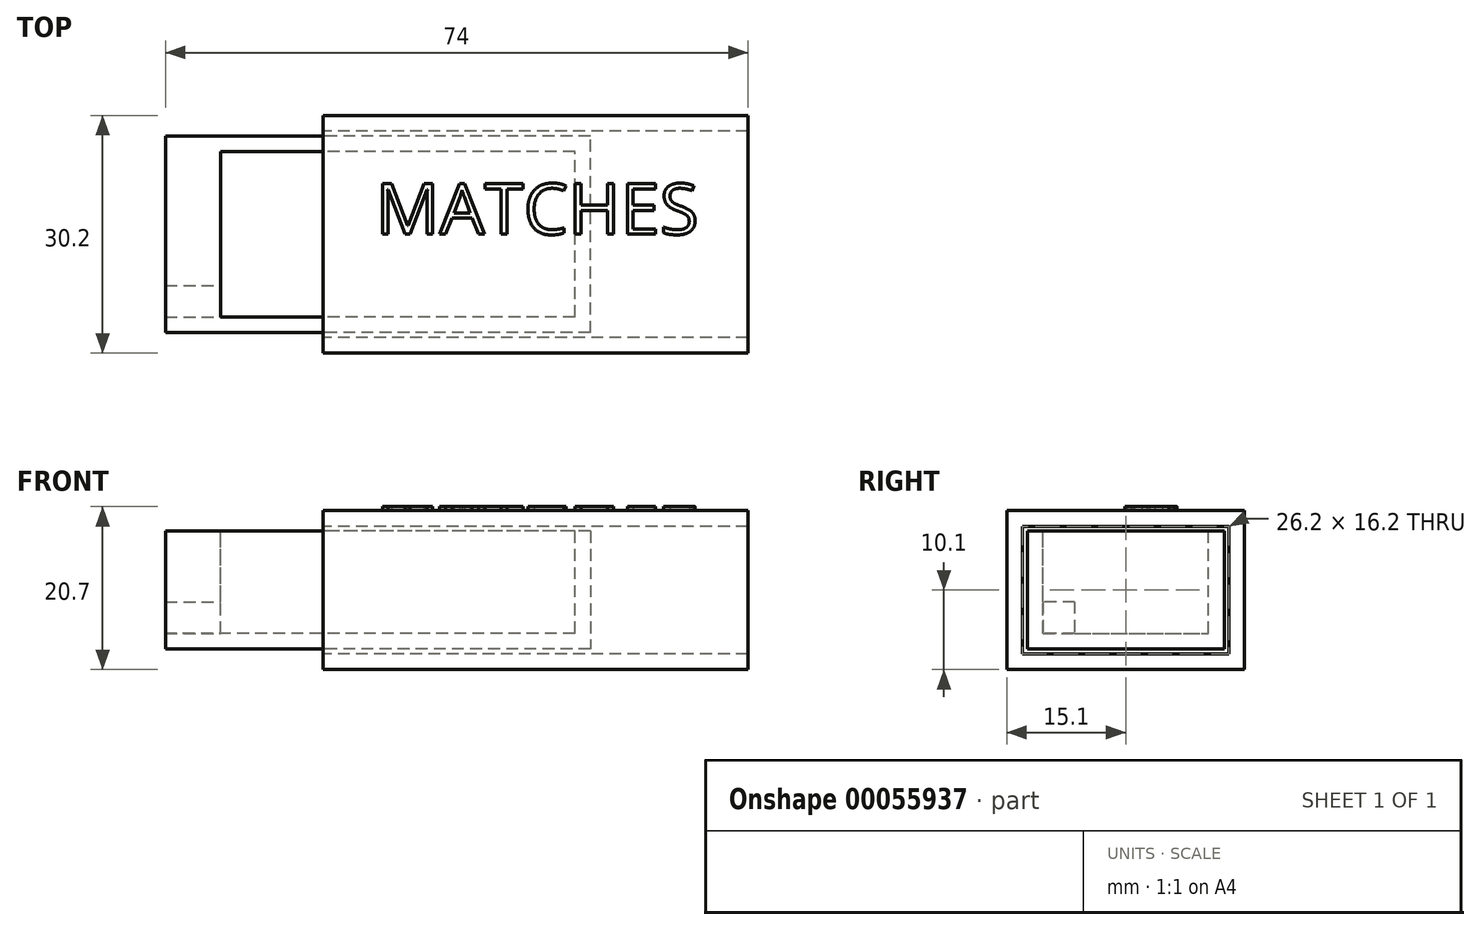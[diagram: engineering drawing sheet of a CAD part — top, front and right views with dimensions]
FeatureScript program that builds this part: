
annotation { "Feature Type Name" : "Feature", "Feature Type Description" : "" }
export const myFeature = defineFeature(function(context is Context, id is Id, definition is map)
    precondition{}
    {
        {
            var Q0;
            Q0=qCreatedBy(makeId("Top.planeOp"),FACE);
            var sketch = newSketch(context, id + "F0", { "sketchPlane" : qUnion([Q0])});
            skLineSegment(sketch, "E0.rect.bottom", {"start": v(27, -12.5) * mm, "end": v(-27, -12.5) * mm});
            skLineSegment(sketch, "E0.rect.top", {"start": v(27, 12.5) * mm, "end": v(-27, 12.5) * mm});
            skLineSegment(sketch, "E0.rect.left", {"start": v(27, -12.5) * mm, "end": v(27, 12.5) * mm});
            skLineSegment(sketch, "E0.rect.right", {"start": v(-27, -12.5) * mm, "end": v(-27, 12.5) * mm});
            skPoint(sketch, "E0.rect.middle", {"position": v(0, 0) * mm});
            skSolve(sketch);
        }
        {
            var Q0;
            Q0 = qSketchRegion(id + "F0", true);
            extrude(context, id + "F1", {"entities" : qUnion([Q0]), "depth" : 15 * mm});
        }
        {
            var Q0;
            Q0=makeQuery(id+"F1.opExtrude","CAP_FACE",FACE,{"disambiguationData":[OSD([sQuery(id+"F0.wireOp",EDGE,"E0.rect.bottom"),sQuery(id+"F0.wireOp",EDGE,"E0.rect.top"),sQuery(id+"F0.wireOp",EDGE,"E0.rect.left"),sQuery(id+"F0.wireOp",EDGE,"E0.rect.right")])],"isStart":false});
            var sketch = newSketch(context, id + "F2", { "sketchPlane" : qUnion([Q0])});
            skLineSegment(sketch, "E1.rect.bottom", {"start": v(25, -10.5) * mm, "end": v(-25, -10.5) * mm});
            skLineSegment(sketch, "E1.rect.top", {"start": v(25, 10.5) * mm, "end": v(-25, 10.5) * mm});
            skLineSegment(sketch, "E1.rect.left", {"start": v(25, -10.5) * mm, "end": v(25, 10.5) * mm});
            skLineSegment(sketch, "E1.rect.right", {"start": v(-25, -10.5) * mm, "end": v(-25, 10.5) * mm});
            skPoint(sketch, "E1.rect.middle", {"position": v(0, 0) * mm});
            skLineSegment(sketch, "E2", {"start": v(25, 0) * mm, "end": v(27, 0) * mm, "construction": true});
            skLineSegment(sketch, "E3", {"start": v(0, 10.5) * mm, "end": v(0, 12.5) * mm, "construction": true});
            skSolve(sketch);
        }
        {
            var Q0;
            Q0 = qSketchRegion(id + "F2", true);
            extrude(context, id + "F3", {"entities" : qUnion([Q0]), "operationType" : NewBodyOperationType.REMOVE, "oppositeDirection" : true, "depth" : 13 * mm});
        }
        {
            var Q0;
            Q0=makeQuery(id+"F3.boolean.opBoolean","COPY",FACE,{"derivedFrom":makeQuery(id+"F3.opExtrude","SWEPT_FACE",FACE,{"disambiguationData":[OSD([sQuery(id+"F2.wireOp",EDGE,"E1.rect.right")])]})});
            var sketch = newSketch(context, id + "F4", { "sketchPlane" : qUnion([Q0])});
            skLineSegment(sketch, "E4.bottom", {"start": v(-10.5, 2) * mm, "end": v(-6.5, 2) * mm});
            skLineSegment(sketch, "E4.top", {"start": v(-10.5, 6) * mm, "end": v(-6.5, 6) * mm});
            skLineSegment(sketch, "E4.left", {"start": v(-10.5, 2) * mm, "end": v(-10.5, 6) * mm});
            skLineSegment(sketch, "E4.right", {"start": v(-6.5, 2) * mm, "end": v(-6.5, 6) * mm});
            skSolve(sketch);
        }
        {
            var Q0;
            Q0 = qSketchRegion(id + "F4", true);
            extrude(context, id + "F5", {"entities" : qUnion([Q0]), "operationType" : NewBodyOperationType.REMOVE, "endBound" : BoundingType.THROUGH_ALL, "oppositeDirection" : true, "depth" : 25 * mm});
        }
        {
            var Q0;
            Q0=makeQuery(id+"F1.opExtrude","SWEPT_FACE",FACE,{"disambiguationData":[OSD([sQuery(id+"F0.wireOp",EDGE,"E0.rect.right")])]});
            var sketch = newSketch(context, id + "F6", { "sketchPlane" : qUnion([Q0])});
            skLineSegment(sketch, "E5.0.0", {"start": v(-12.5, 0) * mm, "end": v(12.5, 0) * mm, "construction": true});
            skLineSegment(sketch, "E5.0.1", {"start": v(12.5, 0) * mm, "end": v(12.5, 15) * mm, "construction": true});
            skLineSegment(sketch, "E5.0.2", {"start": v(12.5, 15) * mm, "end": v(-12.5, 15) * mm});
            skLineSegment(sketch, "E5.0.3", {"start": v(-12.5, 15) * mm, "end": v(-12.5, 0) * mm, "construction": true});
            skLineSegment(sketch, "E6.0", {"start": v(13.1, 15.6) * mm, "end": v(-13.1, 15.6) * mm});
            skLineSegment(sketch, "E6.1", {"start": v(13.1, -0.6) * mm, "end": v(13.1, 15.6) * mm});
            skLineSegment(sketch, "E6.2", {"start": v(-13.1, -0.6) * mm, "end": v(13.1, -0.6) * mm});
            skLineSegment(sketch, "E6.3", {"start": v(-13.1, 15.6) * mm, "end": v(-13.1, -0.6) * mm});
            skLineSegment(sketch, "E7.0", {"start": v(15.1, 17.6) * mm, "end": v(-15.1, 17.6) * mm});
            skLineSegment(sketch, "E7.1", {"start": v(15.1, -2.6) * mm, "end": v(15.1, 17.6) * mm});
            skLineSegment(sketch, "E7.2", {"start": v(-15.1, -2.6) * mm, "end": v(15.1, -2.6) * mm});
            skLineSegment(sketch, "E7.3", {"start": v(-15.1, 17.6) * mm, "end": v(-15.1, -2.6) * mm});
            skSolve(sketch);
        }
        {
            var Q0;
            Q0 = qSketchRegion(id + "F6", true);
            extrude(context, id + "F7", {"entities" : qUnion([Q0]), "oppositeDirection" : true, "depth" : 54 * mm});
        }
        {
            var Q0;
            Q0=makeQuery(id+"F7.opExtrude","SWEPT_FACE",FACE,{"disambiguationData":[OSD([sQuery(id+"F6.wireOp",EDGE,"E7.0")])]});
            var sketch = newSketch(context, id + "F8", { "sketchPlane" : qUnion([Q0])});
            skText(sketch, "E8", { "text": "MATCHES", "fontName": "OpenSans-Regular.ttf"});
            const initialGuessF8  = {"E8": [-0.02028, 0, 1, 0, 0.00647]};
            skSetInitialGuess(sketch, initialGuessF8);
            skSolve(sketch);
        }
        {
            var Q0;
            Q0 = qSketchRegion(id + "F8", true);
            extrude(context, id + "F9", {"entities" : qUnion([Q0]), "operationType" : NewBodyOperationType.ADD, "depth" : .5 * mm});
        }
        {
            var Q0;
            Q0=makeQuery(id+"F7.opExtrude","SWEPT_BODY",BODY,{"disambiguationData":[OSD([sQuery(id+"F6.wireOp",EDGE,"E6.0"),sQuery(id+"F6.wireOp",EDGE,"E6.1"),sQuery(id+"F6.wireOp",EDGE,"E6.2"),sQuery(id+"F6.wireOp",EDGE,"E6.3"),sQuery(id+"F6.wireOp",EDGE,"E7.0"),sQuery(id+"F6.wireOp",EDGE,"E7.1"),sQuery(id+"F6.wireOp",EDGE,"E7.2"),sQuery(id+"F6.wireOp",EDGE,"E7.3")])]});
            transform(context, id + "F10", {"entities" : qUnion([Q0]), "transformType" : TransformType.TRANSLATION_3D, "dx" : 20 * mm, "dy" : 0 * mm, "dz" : 0 * mm, "makeCopy" : false});
        }
        {
            var Q0;
            Q0=makeQuery(id+"F3.boolean.opBoolean","COPY",FACE,{"derivedFrom":makeQuery(id+"F3.opExtrude","SWEPT_FACE",FACE,{"disambiguationData":[OSD([sQuery(id+"F2.wireOp",EDGE,"E1.rect.right")])]})});
            extrude(context, id + "F11", {"entities" : qUnion([Q0]), "operationType" : NewBodyOperationType.ADD, "depth" : 5 * mm});
        }
    });
